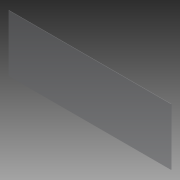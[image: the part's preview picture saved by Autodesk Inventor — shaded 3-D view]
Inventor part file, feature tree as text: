
AUTODESK INVENTOR PART (.ipt)
format: ipt  version: 2013 (Build 170138000, 138)  size: 68,608 bytes
history: native  units: in
note: dims shown in document units (in); Inventor stores cm internally (conversion verified against a paired STEP export)
features: extrude x1, sketch x1
ambient origin geometry x8: Origin, YZ Plane, XZ Plane, XY Plane, X Axis, Y Axis, Z Axis, Center Point
bodies: Solid1 (feature_tree)
feature tree (2):
  extrude  "Extrusion1"  Depth=22.0in
  sketch  "Sketch1"  dims[d0=62.75in d1=22.0in d2=0.125in d3=0.0in]
